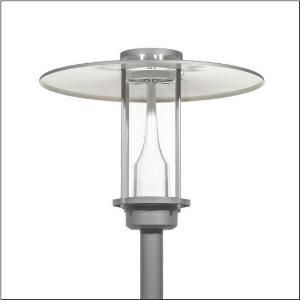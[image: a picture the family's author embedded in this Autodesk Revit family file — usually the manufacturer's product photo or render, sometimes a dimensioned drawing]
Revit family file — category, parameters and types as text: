
# Revit family: city-light_plus_iq___st1_2a_5xa5275mf14hp_2b63
name_source: partatom
category: Lighting Fixtures
units: mm (PartAtom-declared; Revit-internal decimal feet)

## family parameters
Cut with Voids When Loaded = No
Host = Face
Light Source = No
Part Type = Normal
Room Calculation Point = No
Round Connector Dimension = Use Diameter
Shared = No

## types (1)
- --- (1 x LED, 4040 lm, 33.6 W, 2700K)
    Apparent Load = 34 VA
    CIE Flux Codes = 22 60 93 97 100
    Color Rendering = 70
    Color Temperature = 2700K
    Default Elevation = 1800 mm
    Description = City-Light Plus iQ, mast luminaire, Module 540 iQ-SR, primary light control with 3 zone facetted reflector, of plastic, silver coated, highly specular, structured, primary optical cover: cover, of PMMA, transparent, light distribution: ST1.2a, light emission: direct distribution, primary light characteristic: asymmetric, installation type: post-top, LED, High Power LED, rated luminous flux: 4.040lm, luminous efficacy: 120lm/W, light colour: 727, colour temperature: 2700K, control gear: iQ Street-Remote, control: pre-setting: logarithmic dimming characteristic, Street-Remote, Auto-Match, Temp-Guard, Lumen-Switch, Night-Set, Smart-Wire, Light-Fading, Desk-Remote (wireless, voltage-free reading and setting of iQ features in the workshop via application-optimized NFC function/RFID function), optimised constant luminous flux control (CLO 2.0), with terminal, 6-pole, max. 2.5mm², mains connection: 230..240V, AC, 50/60Hz, start of lifetime: 34W, end of service life: 36W, reduction: 15W, luminaire housing, upper part, of glass-fibre reinforced polyester, coated, Siteco® metallic grey (DB 702S), diameter: 750mm, height: 590mm, spigot size: d x l = 76 x 70mm (post-top) | with reducer (optional accessory) 60 x 70mm, mounting height: 3..5m, post-top mast mounting element, of diecast aluminium, coated, Siteco® metallic grey (DB 702S), Module 540 iQ-SR, traffic white (RAL 9016), equipment: Power, protection rating (complete): IP65, insulation class (complete): insulation class II (safety insulation), certification: CE, ENEC, VDE, packaging unit: 1 piece

Light Distribution: ST1.2a
    Height = 590 mm
    Lamp = 1 x LED
    Lamp Light Flux = 4040 lm
    Lamp Power = 33.6 W
    Lamp count = 1
    Length = 750 mm
    Luminous efficacy = 120 lm/W
    Manufacturer = Siteco
    ModVariant = No
    Model = 5XA5275MF14HP
    Mounting Place = Pole
    Mounting Type = Pole top
    Number of Poles = 1
    OnlyDefault = Yes
    Power Factor = 1
    Product Name = City-Light Plus iQ | ST1.2a
    Product group = mast luminaire | pylon top
    ProductGroupID = 6100
    Protection Class = Protection class II
    Protection Degree = IP 65
    RLX_Detail_Level = 1
    RLX_Emergency_Light_Flux = 0 lm
    RLX_Emergency_Type = 0
    RLX_Emergency_Type_DB = No
    RlxData = <blob elided: 52641 chars, md5=9f57c20e>
    Socket = socket
    Standby Power = 0 W
    System Light Flux = 4040 lm
    System Power = 34 W
    Type Comments = factory setting: luminous flux: 100 % | dim-lin: 254 | 695 mA
    Type Image = l_1006456.jpg
    URL = http://relux.com
    VarID = @adj_153893
    Voltage = 0 V
    Weight = 0.00 kg
    Width = 0 mm  [stored 0 ft]

note: [stored X ft] marks values corroborated as IEEE doubles in the binary element streams (Revit-internal decimal feet)

## geometry (parser evidence)
native form markers: Blend x4, Sweep x11
no freeform markers — native parametric forms only
